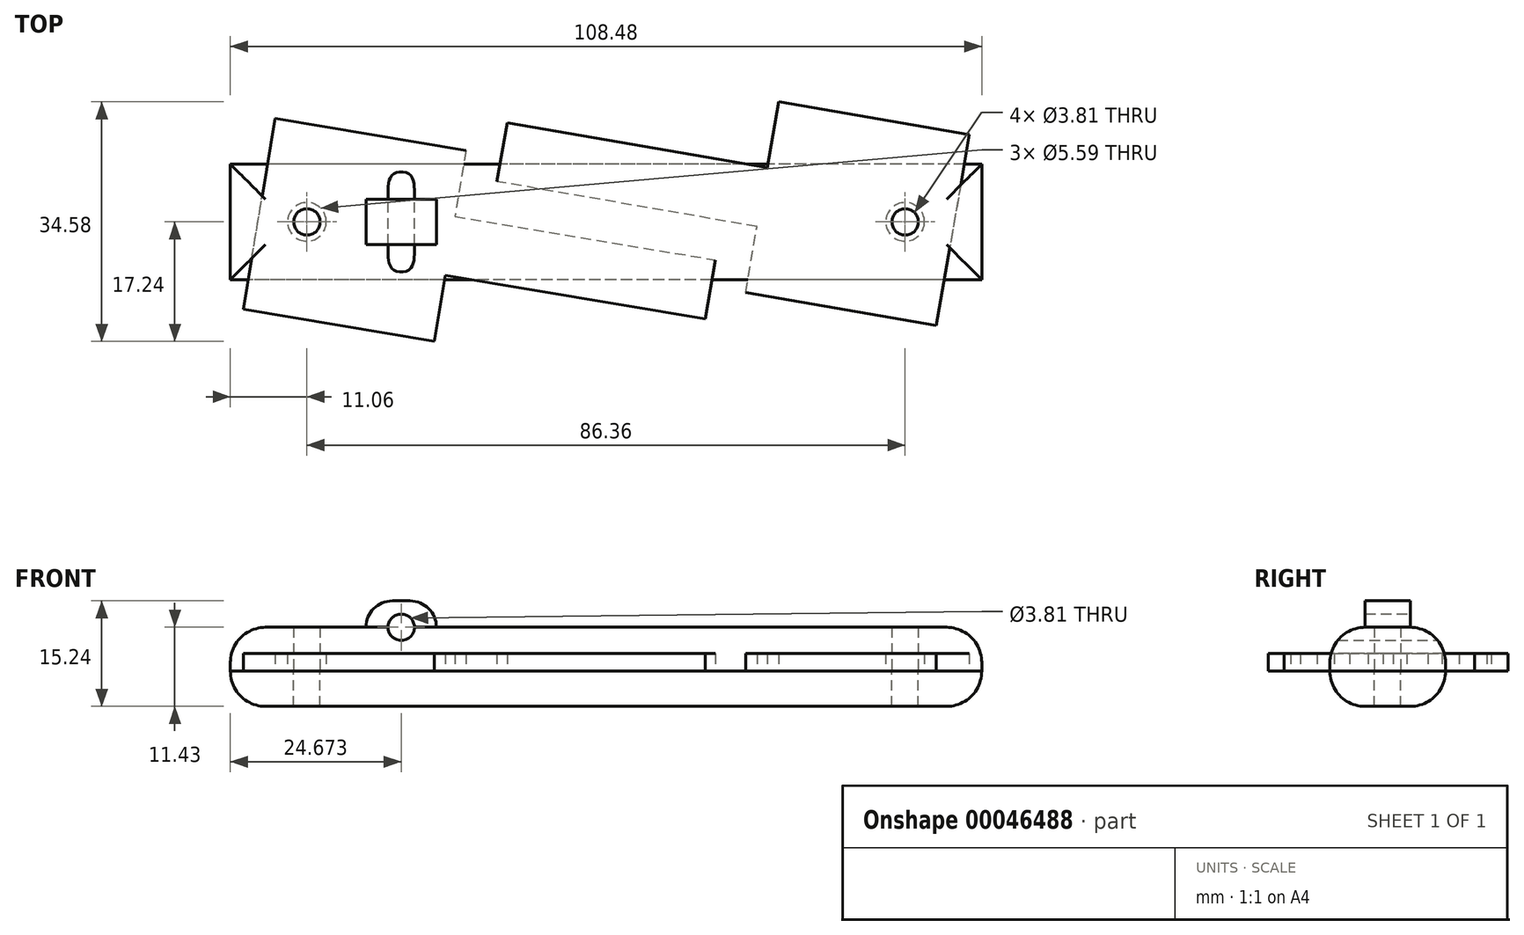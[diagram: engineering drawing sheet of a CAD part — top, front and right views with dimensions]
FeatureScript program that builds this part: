
annotation { "Feature Type Name" : "Feature", "Feature Type Description" : "" }
export const myFeature = defineFeature(function(context is Context, id is Id, definition is map)
    precondition{}
    {
        {
            var Q0;
            Q0=qCreatedBy(makeId("Top.planeOp"),FACE);
            var sketch = newSketch(context, id + "F0", { "sketchPlane" : qUnion([Q0])});
            skLineSegment(sketch, "E0", {"start": v(-47.76, 14.93) * mm, "end": v(-20.2, 10.32) * mm});
            skLineSegment(sketch, "E1", {"start": v(-20.2, 10.32) * mm, "end": v(-21.8, 0.8) * mm});
            skLineSegment(sketch, "E2", {"start": v(-21.8, 0.8) * mm, "end": v(15.78, -5.5) * mm});
            skLineSegment(sketch, "E3", {"start": v(15.78, -5.5) * mm, "end": v(14.35, -14.01) * mm});
            skLineSegment(sketch, "E4", {"start": v(14.35, -14.01) * mm, "end": v(-23.23, -7.72) * mm});
            skLineSegment(sketch, "E5", {"start": v(-23.23, -7.72) * mm, "end": v(-24.82, -17.24) * mm});
            skLineSegment(sketch, "E6", {"start": v(-24.82, -17.24) * mm, "end": v(-52.38, -12.62) * mm});
            skLineSegment(sketch, "E7", {"start": v(-52.38, -12.62) * mm, "end": v(-47.76, 14.93) * mm});
            skLineSegment(sketch, "E8", {"start": v(-50.07, 1.15) * mm, "end": v(-50.07, 1.15) * mm});
            skLineSegment(sketch, "E9", {"start": v(-50.07, 1.15) * mm, "end": v(-43.18, 0) * mm});
            skCircle(sketch, "E10", {"center": v(-43.18, 0) * mm, "radius": 2.8 * mm});
            skPoint(sketch, "E11", {"position": v(-50.07, 1.15) * mm});
            skSolve(sketch);
        }
        {
            var Q0;
            Q0=makeQuery(id+"F0.imprint","IMPRINT",FACE,{"disambiguationData":[TD([[makeQuery(id+"F0.imprint","IMPRINT",EDGE,{"derivedFrom":sQuery(id+"F0.wireOp",EDGE,"E0")}),-1.0]])]});
            extrude(context, id + "F1", {"entities" : qUnion([Q0]), "depth" : 2.54 * mm});
        }
        {
            var Q0;
            Q0=qCreatedBy(makeId("Top.planeOp"),FACE);
            var sketch = newSketch(context, id + "F2", { "sketchPlane" : qUnion([Q0])});
            skLineSegment(sketch, "E12", {"start": v(47.68, -14.96) * mm, "end": v(20.15, -10.19) * mm});
            skLineSegment(sketch, "E13", {"start": v(20.15, -10.19) * mm, "end": v(21.8, -0.68) * mm});
            skLineSegment(sketch, "E14", {"start": v(21.8, -0.68) * mm, "end": v(-15.75, 5.83) * mm});
            skLineSegment(sketch, "E15", {"start": v(-15.75, 5.83) * mm, "end": v(-14.27, 14.33) * mm});
            skLineSegment(sketch, "E16", {"start": v(-14.27, 14.33) * mm, "end": v(23.27, 7.83) * mm});
            skLineSegment(sketch, "E17", {"start": v(23.27, 7.83) * mm, "end": v(24.92, 17.34) * mm});
            skLineSegment(sketch, "E18", {"start": v(24.92, 17.34) * mm, "end": v(52.45, 12.57) * mm});
            skLineSegment(sketch, "E19", {"start": v(52.45, 12.57) * mm, "end": v(47.68, -14.96) * mm});
            skLineSegment(sketch, "E20", {"start": v(50.9, 3.7) * mm, "end": v(50.06, -1.2) * mm});
            skLineSegment(sketch, "E21", {"start": v(50.06, -1.2) * mm, "end": v(43.18, 0) * mm});
            skCircle(sketch, "E22", {"center": v(43.18, 0) * mm, "radius": 2.8 * mm});
            skPoint(sketch, "E23", {"position": v(50.06, -1.2) * mm});
            skSolve(sketch);
        }
        {
            var Q0;
            Q0 = qSketchRegion(id + "F2", true);
            extrude(context, id + "F3", {"entities" : qUnion([Q0]), "depth" : 2.54 * mm});
        }
        {
            var Q0;
            Q0=qCreatedBy(makeId("Top.planeOp"),FACE);
            var sketch = newSketch(context, id + "F4", { "sketchPlane" : qUnion([Q0])});
            skLineSegment(sketch, "E24.rect.bottom", {"start": v(54.24, -8.35) * mm, "end": v(-54.24, -8.35) * mm});
            skLineSegment(sketch, "E24.rect.top", {"start": v(54.24, 8.35) * mm, "end": v(-54.24, 8.35) * mm});
            skLineSegment(sketch, "E24.rect.left", {"start": v(54.24, -8.35) * mm, "end": v(54.24, 8.35) * mm});
            skLineSegment(sketch, "E24.rect.right", {"start": v(-54.24, -8.35) * mm, "end": v(-54.24, 8.35) * mm});
            skPoint(sketch, "E24.rect.middle", {"position": v(0, 0) * mm});
            skCircle(sketch, "E25", {"center": v(-43.18, 0) * mm, "radius": 1.9 * mm});
            skCircle(sketch, "E26", {"center": v(43.18, 0) * mm, "radius": 1.9 * mm});
            skSolve(sketch);
        }
        {
            var Q0;
            Q0=makeQuery(id+"F4.imprint","IMPRINT",FACE,{"disambiguationData":[TD([[makeQuery(id+"F4.imprint","IMPRINT",EDGE,{"derivedFrom":sQuery(id+"F4.wireOp",EDGE,"E24.rect.bottom")}),-1.0]])]});
            extrude(context, id + "F5", {"entities" : qUnion([Q0]), "depth" : 6.35 * mm});
        }
        {
            var Q0;
            Q0 = qSketchRegion(id + "F4", true);
            extrude(context, id + "F6", {"entities" : qUnion([Q0]), "oppositeDirection" : true, "depth" : 5.08 * mm});
        }
        {
            var Q0;
            Q0=makeQuery(id+"F5.opExtrude","CAP_EDGE",EDGE,{"disambiguationData":[OSD([sQuery(id+"F4.wireOp",EDGE,"E24.rect.bottom")])],"isStart":false});
            var Q1;
            Q1=makeQuery(id+"F5.opExtrude","CAP_EDGE",EDGE,{"disambiguationData":[OSD([sQuery(id+"F4.wireOp",EDGE,"E24.rect.left")])],"isStart":false});
            var Q2;
            Q2=makeQuery(id+"F5.opExtrude","CAP_EDGE",EDGE,{"disambiguationData":[OSD([sQuery(id+"F4.wireOp",EDGE,"E24.rect.right")])],"isStart":false});
            var Q3;
            Q3=makeQuery(id+"F5.opExtrude","CAP_EDGE",EDGE,{"disambiguationData":[OSD([sQuery(id+"F4.wireOp",EDGE,"E24.rect.top")])],"isStart":false});
            fillet(context, id + "F7", {"entities" : qUnion([Q0, Q1, Q2, Q3]), "radius" : 5.08 * mm, "tangentPropagation" : true, "allowEdgeOverflow" : false});
        }
        {
            var Q0;
            Q0=makeQuery(id+"F6.opExtrude","CAP_EDGE",EDGE,{"disambiguationData":[OSD([sQuery(id+"F4.wireOp",EDGE,"E24.rect.left")])],"isStart":false});
            var Q1;
            Q1=makeQuery(id+"F6.opExtrude","CAP_EDGE",EDGE,{"disambiguationData":[OSD([sQuery(id+"F4.wireOp",EDGE,"E24.rect.bottom")])],"isStart":false});
            var Q2;
            Q2=makeQuery(id+"F6.opExtrude","CAP_EDGE",EDGE,{"disambiguationData":[OSD([sQuery(id+"F4.wireOp",EDGE,"E24.rect.right")])],"isStart":false});
            var Q3;
            Q3=makeQuery(id+"F6.opExtrude","CAP_EDGE",EDGE,{"disambiguationData":[OSD([sQuery(id+"F4.wireOp",EDGE,"E24.rect.top")])],"isStart":false});
            fillet(context, id + "F8", {"entities" : qUnion([Q0, Q1, Q2, Q3]), "radius" : 5.08 * mm, "tangentPropagation" : true, "allowEdgeOverflow" : false});
        }
        {
            var Q0;
            Q0=makeQuery(id+"F5.opExtrude","CAP_FACE",FACE,{"disambiguationData":[OSD([sQuery(id+"F4.wireOp",EDGE,"E24.rect.bottom"),sQuery(id+"F4.wireOp",EDGE,"E24.rect.top"),sQuery(id+"F4.wireOp",EDGE,"E24.rect.left"),sQuery(id+"F4.wireOp",EDGE,"E24.rect.right"),sQuery(id+"F4.wireOp",EDGE,"E25"),sQuery(id+"F4.wireOp",EDGE,"E26")])],"isStart":false});
            var sketch = newSketch(context, id + "F9", { "sketchPlane" : qUnion([Q0])});
            skLineSegment(sketch, "E27.rect.bottom", {"start": v(-24.49, -3.27) * mm, "end": v(-34.65, -3.27) * mm});
            skLineSegment(sketch, "E27.rect.top", {"start": v(-24.49, 3.27) * mm, "end": v(-34.65, 3.27) * mm});
            skLineSegment(sketch, "E27.rect.left", {"start": v(-24.49, -3.27) * mm, "end": v(-24.49, 3.27) * mm});
            skLineSegment(sketch, "E27.rect.right", {"start": v(-34.65, -3.27) * mm, "end": v(-34.65, 3.27) * mm});
            skPoint(sketch, "E27.rect.middle", {"position": v(-29.57, 0) * mm});
            skSolve(sketch);
        }
        {
            var Q0;
            Q0=makeQuery(id+"F9.imprint","IMPRINT",FACE,{"disambiguationData":[TD([[makeQuery(id+"F9.imprint","IMPRINT",EDGE,{"derivedFrom":sQuery(id+"F9.wireOp",EDGE,"E27.rect.bottom")}),1.0]])]});
            extrude(context, id + "F10", {"entities" : qUnion([Q0]), "operationType" : NewBodyOperationType.ADD, "depth" : 3.8 * mm});
        }
        {
            var Q0;
            Q0=makeQuery(id+"F10.opExtrude","CAP_EDGE",EDGE,{"disambiguationData":[OSD([sQuery(id+"F9.wireOp",EDGE,"E27.rect.right")])],"isStart":false});
            var Q1;
            Q1=makeQuery(id+"F10.opExtrude","CAP_EDGE",EDGE,{"disambiguationData":[OSD([sQuery(id+"F9.wireOp",EDGE,"E27.rect.left")])],"isStart":false});
            fillet(context, id + "F11", {"entities" : qUnion([Q0, Q1]), "radius" : 3.8 * mm, "tangentPropagation" : true, "allowEdgeOverflow" : false});
        }
        {
            var Q0;
            Q0=makeQuery(id+"F10.opExtrude","SWEPT_FACE",FACE,{"disambiguationData":[OSD([sQuery(id+"F9.wireOp",EDGE,"E27.rect.top")])]});
            var sketch = newSketch(context, id + "F12", { "sketchPlane" : qUnion([Q0])});
            skPoint(sketch, "E28", {"position": v(29.57, 6.35) * mm});
            skSolve(sketch);
        }
        {
            var Q0;
            Q0=sQuery(id+"F12.wireOp",VERTEX,"E28");
            var Q1;
            Q1=makeQuery(id+"F5.opExtrude","SWEPT_BODY",BODY,{"disambiguationData":[OSD([sQuery(id+"F4.wireOp",EDGE,"E24.rect.bottom"),sQuery(id+"F4.wireOp",EDGE,"E24.rect.top"),sQuery(id+"F4.wireOp",EDGE,"E24.rect.left"),sQuery(id+"F4.wireOp",EDGE,"E24.rect.right"),sQuery(id+"F4.wireOp",EDGE,"E25"),sQuery(id+"F4.wireOp",EDGE,"E26")])]});
            hole(context, id + "F13", {"style" : HoleStyle.SIMPLE, "holeDiameter" : 3.8 * mm, "endStyle" : HoleEndStyle.THROUGH, "locations" : qUnion([Q0]), "scope" : qUnion([Q1]), "isTappedThrough" : true});
        }
        {
            var Q0;
            Q0=sQuery(id+"F12.wireOp",VERTEX,"E28");
            var Q1;
            Q1=makeQuery(id+"F5.opExtrude","SWEPT_BODY",BODY,{"disambiguationData":[OSD([sQuery(id+"F4.wireOp",EDGE,"E24.rect.bottom"),sQuery(id+"F4.wireOp",EDGE,"E24.rect.top"),sQuery(id+"F4.wireOp",EDGE,"E24.rect.left"),sQuery(id+"F4.wireOp",EDGE,"E24.rect.right"),sQuery(id+"F4.wireOp",EDGE,"E25"),sQuery(id+"F4.wireOp",EDGE,"E26")])]});
            hole(context, id + "F14", {"style" : HoleStyle.SIMPLE, "holeDiameter" : 3.8 * mm, "endStyle" : HoleEndStyle.THROUGH, "oppositeDirection" : true, "locations" : qUnion([Q0]), "scope" : qUnion([Q1])});
        }
        {
            var Q0;
            Q0=makeQuery(id+"F1.opExtrude","SWEPT_BODY",BODY,{"disambiguationData":[OSD([sQuery(id+"F0.wireOp",EDGE,"E0"),sQuery(id+"F0.wireOp",EDGE,"E1"),sQuery(id+"F0.wireOp",EDGE,"E2"),sQuery(id+"F0.wireOp",EDGE,"E3"),sQuery(id+"F0.wireOp",EDGE,"E4"),sQuery(id+"F0.wireOp",EDGE,"E5"),sQuery(id+"F0.wireOp",EDGE,"E6"),sQuery(id+"F0.wireOp",EDGE,"E7"),sQuery(id+"F0.wireOp",EDGE,"00a381d7-7105-4c5e-a130-2b6659f4c8b5")])]});
            transform(context, id + "F15", {"entities" : qUnion([Q0]), "transformType" : TransformType.TRANSLATION_3D, "dx" : 0 * mm, "dy" : 0 * mm, "dz" : 0 * mm, "makeCopy" : true});
        }
    });
